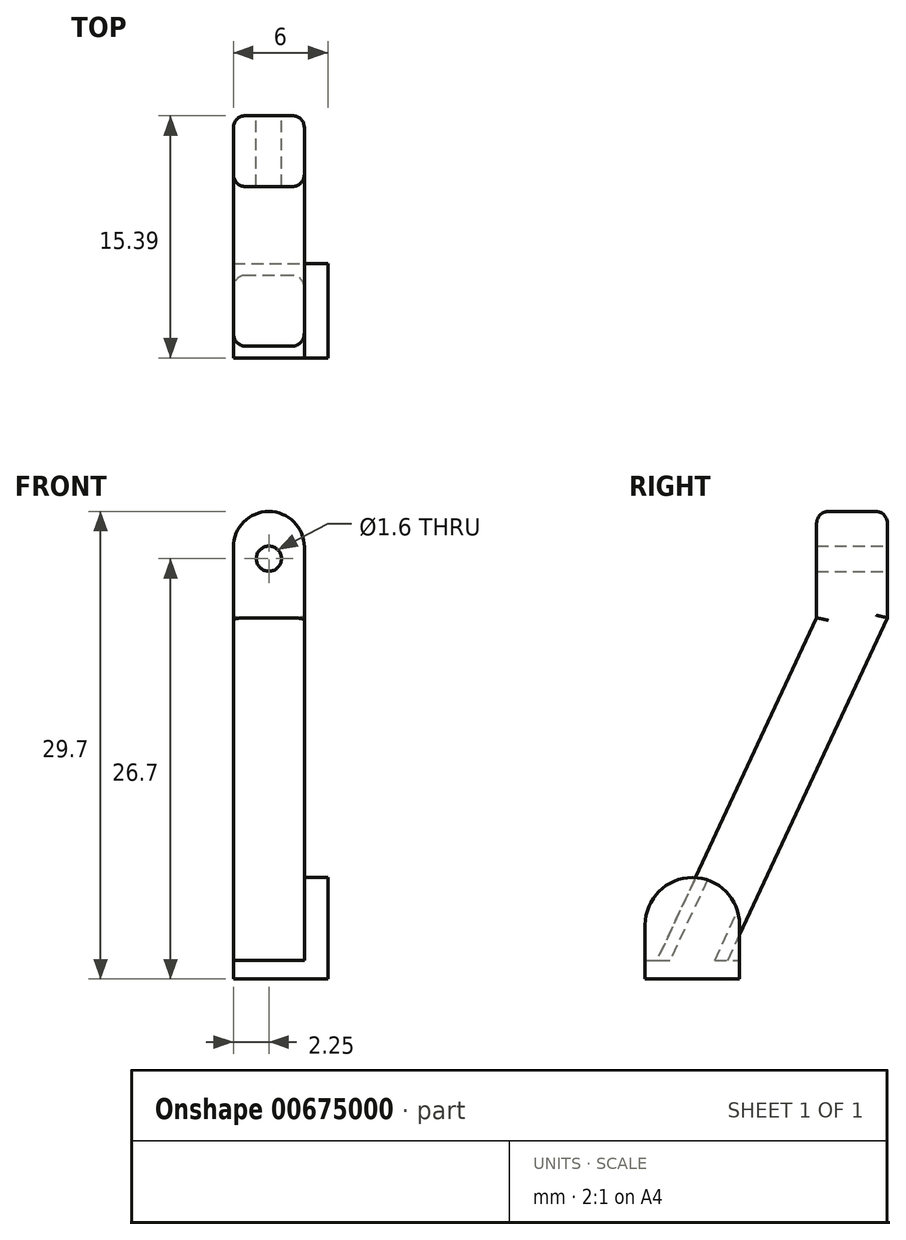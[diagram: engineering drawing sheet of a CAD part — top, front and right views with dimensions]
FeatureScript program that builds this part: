
annotation { "Feature Type Name" : "Feature", "Feature Type Description" : "" }
export const myFeature = defineFeature(function(context is Context, id is Id, definition is map)
    precondition{}
    {
        {
            assignVariable(context, id + "F0", {"name" : "Faktor", "anyValue" : 1.5});
        }
        {
            var Q0;
            Q0=qCreatedBy(makeId("Top.planeOp"),FACE);
            var sketch = newSketch(context, id + "F1", { "sketchPlane" : qUnion([Q0])});
            skLineSegment(sketch, "E0.bottom", {"start": v(1.5, 0) * mm, "end": v(7.5, 0) * mm});
            skLineSegment(sketch, "E0.top", {"start": v(1.5, 6) * mm, "end": v(7.5, 6) * mm});
            skLineSegment(sketch, "E0.left", {"start": v(1.5, 0) * mm, "end": v(1.5, 6) * mm});
            skLineSegment(sketch, "E0.right", {"start": v(7.5, 0) * mm, "end": v(7.5, 6) * mm});
            skSolve(sketch);
        }
        {
            var Q0;
            Q0=qSketchRegion(id+"F1",true);
            extrude(context, id + "F2", {"entities" : qUnion([Q0]), "depth" : getVariable(context, 'Faktor') * 0.8 * mm, "offsetDistance" : 25 * mm});
        }
        {
            var Q0;
            Q0=qCreatedBy(makeId("Right.planeOp"),FACE);
            cPlane(context, id + "F3", {"entities" : qUnion([Q0]), "cplaneType" : CPlaneType.OFFSET, "offset" : getVariable(context, 'Faktor') * 2.5 * mm, "width" : 150 * mm, "height" : 150 * mm});
        }
        {
            var Q0;
            Q0=qCreatedBy(id+"F3.planeOp",FACE);
            var sketch = newSketch(context, id + "F4", { "sketchPlane" : qUnion([Q0])});
            skLineSegment(sketch, "E1", {"start": v(5.25, 1.2) * mm, "end": v(15.4, 22.95) * mm});
            skLineSegment(sketch, "E2", {"start": v(10.9, 22.95) * mm, "end": v(0.75, 1.2) * mm});
            skLineSegment(sketch, "E3", {"start": v(0.75, 1.2) * mm, "end": v(5.25, 1.2) * mm});
            skLineSegment(sketch, "E4", {"start": v(10.9, 22.95) * mm, "end": v(10.9, 29.7) * mm});
            skLineSegment(sketch, "E5", {"start": v(10.9, 29.7) * mm, "end": v(15.4, 29.7) * mm});
            skLineSegment(sketch, "E6", {"start": v(15.4, 29.7) * mm, "end": v(15.4, 22.95) * mm});
            skLineSegment(sketch, "E7", {"start": v(10.9, 22.95) * mm, "end": v(18.63, 22.95) * mm, "construction": true});
            skSolve(sketch);
        }
        {
            var Q0;
            Q0=qSketchRegion(id+"F4",true);
            extrude(context, id + "F5", {"entities" : qUnion([Q0]), "operationType" : NewBodyOperationType.ADD, "endBound" : BoundingType.SYMMETRIC, "depth" : getVariable(context, 'Faktor') * 3 * mm, "offsetDistance" : 25 * mm});
        }
        {
            var Q0;
            Q0=makeQuery(id+"F5.opExtrude","SWEPT_FACE",FACE,{"disambiguationData":[OSD([sQuery(id+"F4.wireOp",EDGE,"E6")])]});
            var sketch = newSketch(context, id + "F6", { "sketchPlane" : qUnion([Q0])});
            skCircle(sketch, "E8", {"center": v(-3.75, 26.7) * mm, "radius": 0.8 * mm});
            skSolve(sketch);
        }
        {
            var Q0;
            Q0=qSketchRegion(id+"F6",true);
            extrude(context, id + "F7", {"entities" : qUnion([Q0]), "operationType" : NewBodyOperationType.REMOVE, "endBound" : BoundingType.THROUGH_ALL, "oppositeDirection" : true, "depth" : 25 * mm, "offsetDistance" : 25 * mm});
        }
        {
            var Q0;
            Q0=makeQuery(id+"F5.opExtrude","CAP_EDGE",EDGE,{"disambiguationData":[OSD([sQuery(id+"F4.wireOp",EDGE,"E5")])],"isStart":true});
            var Q1;
            Q1=makeQuery(id+"F5.opExtrude","CAP_EDGE",EDGE,{"disambiguationData":[OSD([sQuery(id+"F4.wireOp",EDGE,"E5")])],"isStart":false});
            fillet(context, id + "F8", {"entities" : qUnion([Q0, Q1]), "radius" : getVariable(context, 'Faktor') * 1.5 * mm, "tangentPropagation" : true, "allowEdgeOverflow" : false});
        }
        {
            var Q0;
            Q0=makeQuery(id+"F5.opExtrude","CAP_EDGE",EDGE,{"disambiguationData":[OSD([sQuery(id+"F4.wireOp",EDGE,"E1")])],"isStart":true});
            var Q1;
            Q1=makeQuery(id+"F5.opExtrude","CAP_EDGE",EDGE,{"disambiguationData":[OSD([sQuery(id+"F4.wireOp",EDGE,"E6")])],"isStart":true});
            var Q2;
            Q2=makeQuery(id+"F8.opFillet","BLEND_EDGE",EDGE,{"blendedFrom":[makeQuery(id+"F5.opExtrude","CAP_EDGE",EDGE,{"disambiguationData":[OSD([sQuery(id+"F4.wireOp",EDGE,"E5")])],"isStart":false}),makeQuery(id+"F5.opExtrude","SWEPT_FACE",FACE,{"disambiguationData":[OSD([sQuery(id+"F4.wireOp",EDGE,"E6")])]})],"blendedInto":[makeQuery(id+"F5.opExtrude","SWEPT_FACE",FACE,{"disambiguationData":[OSD([sQuery(id+"F4.wireOp",EDGE,"E6")])]})]});
            var Q3;
            Q3=makeQuery(id+"F5.opExtrude","CAP_EDGE",EDGE,{"disambiguationData":[OSD([sQuery(id+"F4.wireOp",EDGE,"E1")])],"isStart":false});
            var Q4;
            Q4=makeQuery(id+"F5.opExtrude","CAP_EDGE",EDGE,{"disambiguationData":[OSD([sQuery(id+"F4.wireOp",EDGE,"E2")])],"isStart":true});
            var Q5;
            Q5=makeQuery(id+"F5.opExtrude","CAP_EDGE",EDGE,{"disambiguationData":[OSD([sQuery(id+"F4.wireOp",EDGE,"E4")])],"isStart":true});
            var Q6;
            Q6=makeQuery(id+"F5.opExtrude","CAP_EDGE",EDGE,{"disambiguationData":[OSD([sQuery(id+"F4.wireOp",EDGE,"E2")])],"isStart":false});
            fillet(context, id + "F9", {"entities" : qUnion([Q0, Q1, Q2, Q3, Q4, Q5, Q6]), "radius" : getVariable(context, 'Faktor') * 0.5 * mm, "tangentPropagation" : true, "allowEdgeOverflow" : false});
        }
        {
            var Q0;
            Q0=makeQuery(id+"F2.opExtrude","SWEPT_FACE",FACE,{"disambiguationData":[OSD([sQuery(id+"F1.wireOp",EDGE,"E0.right")])]});
            var sketch = newSketch(context, id + "F10", { "sketchPlane" : qUnion([Q0])});
            skLineSegment(sketch, "E9.bottom", {"start": v(0, 1.2) * mm, "end": v(6, 1.2) * mm});
            skLineSegment(sketch, "E9.left", {"start": v(0, 1.2) * mm, "end": v(0, 3.45) * mm});
            skLineSegment(sketch, "E9.right", {"start": v(6, 1.2) * mm, "end": v(6, 3.45) * mm});
            skArc(sketch, "E10", {"start": v(6, 3.45) * mm, "mid": v(3, 6.45) * mm, "end": v(0, 3.45) * mm});
            skSolve(sketch);
        }
        {
            var Q0;
            Q0=qSketchRegion(id+"F10",true);
            extrude(context, id + "F11", {"entities" : qUnion([Q0]), "operationType" : NewBodyOperationType.ADD, "oppositeDirection" : true, "depth" : getVariable(context, 'Faktor') * 1 * mm, "offsetDistance" : 25 * mm});
        }
    });
